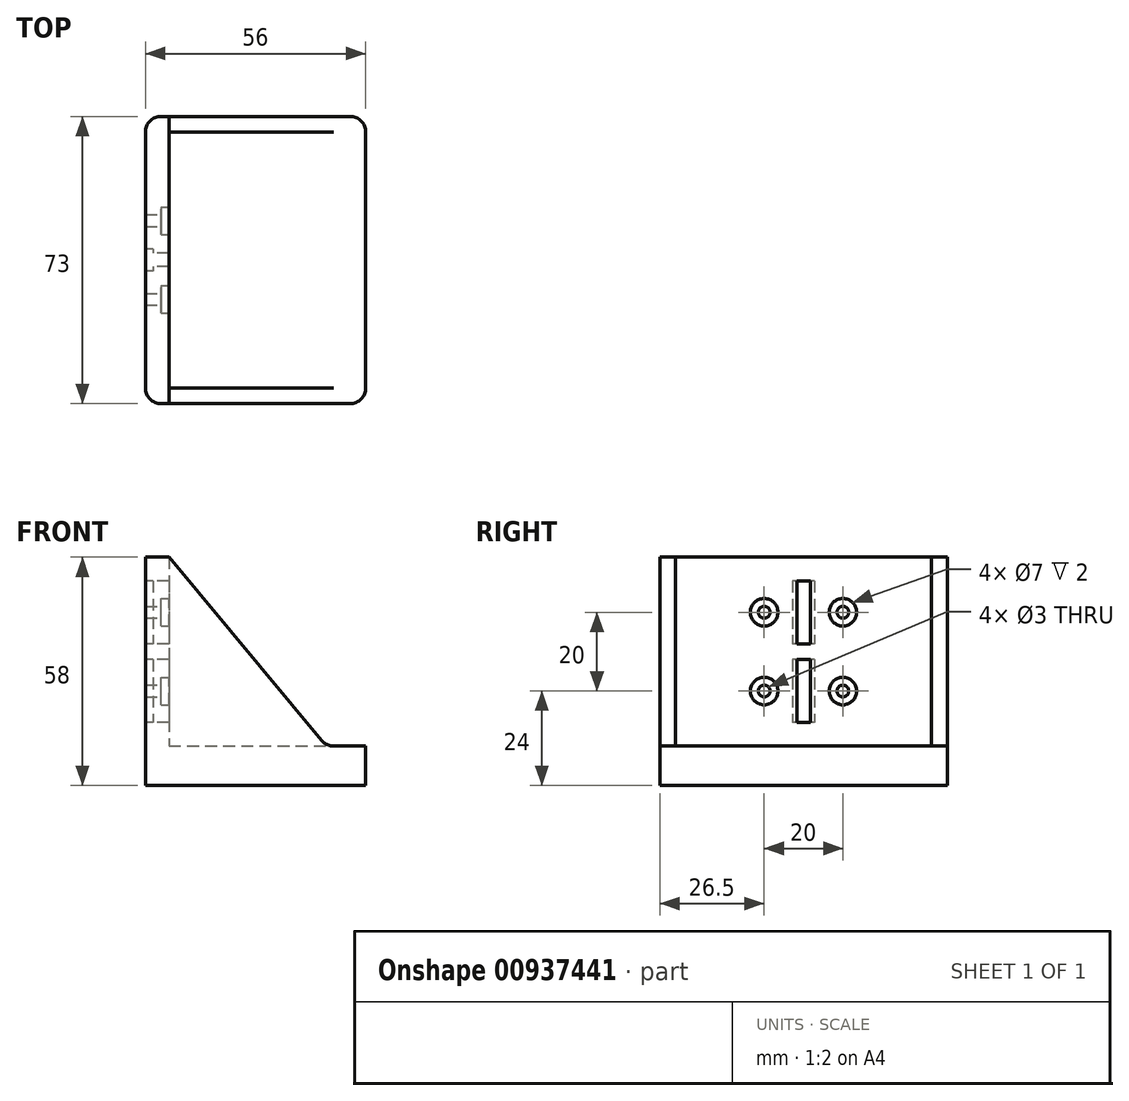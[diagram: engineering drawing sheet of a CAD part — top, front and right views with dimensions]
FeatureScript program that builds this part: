
annotation { "Feature Type Name" : "Feature", "Feature Type Description" : "" }
export const myFeature = defineFeature(function(context is Context, id is Id, definition is map)
    precondition{}
    {
        {
            var Q0;
            Q0=qCreatedBy(makeId("Top.planeOp"),FACE);
            var sketch = newSketch(context, id + "F0", { "sketchPlane" : qUnion([Q0])});
            skLineSegment(sketch, "E0.bottom", {"start": v(0, 73) * mm, "end": v(56, 73) * mm});
            skLineSegment(sketch, "E0.top", {"start": v(0, 0) * mm, "end": v(56, 0) * mm});
            skLineSegment(sketch, "E0.left", {"start": v(0, 73) * mm, "end": v(0, 0) * mm});
            skLineSegment(sketch, "E0.right", {"start": v(56, 73) * mm, "end": v(56, 0) * mm});
            skSolve(sketch);
        }
        {
            var Q0;
            Q0=qSketchRegion(id+"F0",true);
            extrude(context, id + "F1", {"entities" : qUnion([Q0]), "depth" : 10 * mm, "offsetDistance" : 25 * mm});
        }
        {
            var Q0;
            Q0=makeQuery(id+"F1.opExtrude","CAP_FACE",FACE,{"disambiguationData":[OSD([sQuery(id+"F0.wireOp",EDGE,"JcqLtr4a-4iO0-7SYc-JrXt-3wWf4lI9VCyy"),sQuery(id+"F0.wireOp",EDGE,"3zeIyssa-BI9L-WOF6-APSg-kyZtDzQDufFM"),sQuery(id+"F0.wireOp",EDGE,"Hb38dC7V-6ZDo-NrQG-Z8Se-XjxkW8JbUmMz"),sQuery(id+"F0.wireOp",EDGE,"y3aIqdCw-jFc2-MhhD-7X5v-KuRHTVy27k4Q"),sQuery(id+"F0.wireOp",EDGE,"XVNT8TL3-6rPS-E8CT-cUIb-nR5d3DAh4WGq"),sQuery(id+"F0.wireOp",EDGE,"E0.bottom"),sQuery(id+"F0.wireOp",EDGE,"E0.top"),sQuery(id+"F0.wireOp",EDGE,"E0.left"),sQuery(id+"F0.wireOp",EDGE,"E0.right")])],"isStart":false});
            var sketch = newSketch(context, id + "F2", { "sketchPlane" : qUnion([Q0])});
            skLineSegment(sketch, "E1.bottom", {"start": v(0, 73) * mm, "end": v(6, 73) * mm});
            skLineSegment(sketch, "E1.top", {"start": v(0, 0) * mm, "end": v(6, 0) * mm});
            skLineSegment(sketch, "E1.left", {"start": v(0, 73) * mm, "end": v(0, 0) * mm});
            skLineSegment(sketch, "E1.right", {"start": v(6, 73) * mm, "end": v(6, 0) * mm});
            skLineSegment(sketch, "E2.bottom", {"start": v(6, 73) * mm, "end": v(46, 73) * mm});
            skLineSegment(sketch, "E2.top", {"start": v(6, 69) * mm, "end": v(46, 69) * mm});
            skLineSegment(sketch, "E2.left", {"start": v(6, 73) * mm, "end": v(6, 69) * mm});
            skLineSegment(sketch, "E2.right", {"start": v(46, 73) * mm, "end": v(46, 69) * mm});
            skLineSegment(sketch, "E3.bottom", {"start": v(6, 0) * mm, "end": v(46, 0) * mm});
            skLineSegment(sketch, "E3.top", {"start": v(6, 4) * mm, "end": v(46, 4) * mm});
            skLineSegment(sketch, "E3.left", {"start": v(6, 0) * mm, "end": v(6, 4) * mm});
            skLineSegment(sketch, "E3.right", {"start": v(46, 0) * mm, "end": v(46, 4) * mm});
            skSolve(sketch);
        }
        {
            var Q0;
            Q0=qSketchRegion(id+"F2",true);
            extrude(context, id + "F3", {"entities" : qUnion([Q0]), "operationType" : NewBodyOperationType.ADD, "depth" : (25 + 15 + 8) * mm, "offsetDistance" : 25 * mm});
        }
        {
            var Q0;
            Q0=makeQuery(id+"F3.boolean.opBoolean","MERGE",FACE,{"derivedFrom":[makeQuery(id+"F1.opExtrude","SWEPT_FACE",FACE,{"disambiguationData":[OSD([sQuery(id+"F0.wireOp",EDGE,"E0.top")])]}),makeQuery(id+"F3.opExtrude","SWEPT_FACE",FACE,{"disambiguationData":[OSD([sQuery(id+"F2.wireOp",EDGE,"E1.top"),sQuery(id+"F2.wireOp",EDGE,"E3.bottom")])]})]});
            var sketch = newSketch(context, id + "F4", { "sketchPlane" : qUnion([Q0])});
            skLineSegment(sketch, "E4", {"start": v(46, 10) * mm, "end": v(6, 58) * mm});
            skLineSegment(sketch, "E5", {"start": v(6, 58) * mm, "end": v(46, 58) * mm});
            skLineSegment(sketch, "E6", {"start": v(46, 58) * mm, "end": v(46, 10) * mm});
            skSolve(sketch);
        }
        {
            var Q0;
            Q0=qSketchRegion(id+"F4",true);
            extrude(context, id + "F5", {"entities" : qUnion([Q0]), "operationType" : NewBodyOperationType.REMOVE, "endBound" : BoundingType.THROUGH_ALL, "oppositeDirection" : true, "depth" : 25 * mm, "offsetDistance" : 25 * mm});
        }
        {
            var Q0;
            Q0=makeQuery(id+"F3.boolean.opBoolean","MERGE",EDGE,{"derivedFrom":[makeQuery(id+"F1.opExtrude","SWEPT_EDGE",EDGE,{"disambiguationData":[OSD([sQuery(id+"F0.wireOp",EDGE,"E0.top"),sQuery(id+"F0.wireOp",EDGE,"E0.left")])]}),makeQuery(id+"F3.opExtrude","SWEPT_EDGE",EDGE,{"disambiguationData":[OSD([sQuery(id+"F2.wireOp",EDGE,"E1.top"),sQuery(id+"F2.wireOp",EDGE,"E1.left")])]})]});
            var Q1;
            Q1=makeQuery(id+"F1.opExtrude","SWEPT_EDGE",EDGE,{"disambiguationData":[OSD([sQuery(id+"F0.wireOp",EDGE,"E0.top"),sQuery(id+"F0.wireOp",EDGE,"E0.right")])]});
            var Q2;
            Q2=makeQuery(id+"F5.boolean.opBoolean","MERGE",EDGE,{"derivedFrom":[makeQuery(id+"F3.opExtrude","CAP_EDGE",EDGE,{"disambiguationData":[OSD([sQuery(id+"F2.wireOp",EDGE,"E3.right")])],"isStart":true})],"fromTools":[makeQuery(id+"F5.opExtrude","SWEPT_EDGE",EDGE,{"disambiguationData":[OSD([sQuery(id+"F0.wireOp",EDGE,"E0.top"),sQuery(id+"F4.wireOp",EDGE,"E4"),sQuery(id+"F4.wireOp",EDGE,"E6")])]})]});
            var Q3;
            Q3=makeQuery(id+"F5.boolean.opBoolean","MERGE",EDGE,{"derivedFrom":[makeQuery(id+"F3.opExtrude","CAP_EDGE",EDGE,{"disambiguationData":[OSD([sQuery(id+"F2.wireOp",EDGE,"E2.right")])],"isStart":true})],"fromTools":[makeQuery(id+"F5.opExtrude","SWEPT_EDGE",EDGE,{"disambiguationData":[OSD([sQuery(id+"F0.wireOp",EDGE,"E0.top"),sQuery(id+"F4.wireOp",EDGE,"E4"),sQuery(id+"F4.wireOp",EDGE,"E6")])]})]});
            var Q4;
            Q4=makeQuery(id+"F1.opExtrude","SWEPT_EDGE",EDGE,{"disambiguationData":[OSD([sQuery(id+"F0.wireOp",EDGE,"E0.bottom"),sQuery(id+"F0.wireOp",EDGE,"E0.right")])]});
            var Q5;
            Q5=makeQuery(id+"F3.boolean.opBoolean","MERGE",EDGE,{"derivedFrom":[makeQuery(id+"F1.opExtrude","SWEPT_EDGE",EDGE,{"disambiguationData":[OSD([sQuery(id+"F0.wireOp",EDGE,"E0.bottom"),sQuery(id+"F0.wireOp",EDGE,"E0.left")])]}),makeQuery(id+"F3.opExtrude","SWEPT_EDGE",EDGE,{"disambiguationData":[OSD([sQuery(id+"F2.wireOp",EDGE,"E1.bottom"),sQuery(id+"F2.wireOp",EDGE,"E1.left")])]})]});
            fillet(context, id + "F6", {"entities" : qUnion([Q0, Q1, Q2, Q3, Q4, Q5]), "radius" : 4 * mm, "tangentPropagation" : true, "allowEdgeOverflow" : false});
        }
        {
            var Q0;
            Q0=makeQuery(id+"F3.boolean.opBoolean","MERGE",FACE,{"derivedFrom":[makeQuery(id+"F1.opExtrude","SWEPT_FACE",FACE,{"disambiguationData":[OSD([sQuery(id+"F0.wireOp",EDGE,"E0.left")])]}),makeQuery(id+"F3.opExtrude","SWEPT_FACE",FACE,{"disambiguationData":[OSD([sQuery(id+"F2.wireOp",EDGE,"E1.left")])]})]});
            var sketch = newSketch(context, id + "F7", { "sketchPlane" : qUnion([Q0])});
            skLineSegment(sketch, "E7", {"start": v(-36.5, 52) * mm, "end": v(-36.5, 16) * mm, "construction": true});
            skLineSegment(sketch, "E8", {"start": v(-38.22, 52) * mm, "end": v(-38.22, 16) * mm});
            skLineSegment(sketch, "E9", {"start": v(-34.77, 52) * mm, "end": v(-34.77, 16) * mm});
            skLineSegment(sketch, "E10.bottom", {"start": v(-39.26, 36) * mm, "end": v(-33.74, 36) * mm});
            skLineSegment(sketch, "E10.top", {"start": v(-39.26, 32) * mm, "end": v(-33.74, 32) * mm});
            skLineSegment(sketch, "E10.left", {"start": v(-39.26, 36) * mm, "end": v(-39.26, 32) * mm});
            skLineSegment(sketch, "E10.right", {"start": v(-33.74, 36) * mm, "end": v(-33.74, 32) * mm});
            skLineSegment(sketch, "E11", {"start": v(-36.5, 34) * mm, "end": v(-39.26, 34) * mm, "construction": true});
            skLineSegment(sketch, "E12", {"start": v(-34.77, 52) * mm, "end": v(-38.22, 52) * mm});
            skLineSegment(sketch, "E13", {"start": v(-34.77, 16) * mm, "end": v(-38.22, 16) * mm});
            skLineSegment(sketch, "E14.bottom", {"start": v(-39.26, 52) * mm, "end": v(-33.74, 52) * mm});
            skLineSegment(sketch, "E14.top", {"start": v(-39.26, 16) * mm, "end": v(-33.74, 16) * mm});
            skLineSegment(sketch, "E14.left", {"start": v(-39.26, 52) * mm, "end": v(-39.26, 16) * mm});
            skLineSegment(sketch, "E14.right", {"start": v(-33.74, 52) * mm, "end": v(-33.74, 16) * mm});
            skLineSegment(sketch, "E15", {"start": v(-39.26, 34) * mm, "end": v(-39.26, 34) * mm});
            skLineSegment(sketch, "E16", {"start": v(-36.5, 58) * mm, "end": v(-36.5, 52) * mm, "construction": true});
            skSolve(sketch);
        }
        {
            var Q0;
            {var subQ0=sQuery(id+"F7.wireOp",EDGE,"E14.bottom");var subQ1=sQuery(id+"F7.wireOp",EDGE,"E8");var subQ2=makeQuery(id+"F7.imprint","INTERSECT",VERTEX,{"derivedFrom":[subQ1,subQ0]});Q0=makeQuery(id+"F7.imprint","IMPRINT",FACE,{"disambiguationData":[TD([[makeQuery(id+"F7.imprint","IMPRINT",EDGE,{"disambiguationData":[TD([[subQ2,-1.0]])],"derivedFrom":subQ1}),-1.0]])]});}
            var Q1;
            {var subQ0=sQuery(id+"F7.wireOp",EDGE,"E14.bottom");var subQ1=sQuery(id+"F7.wireOp",EDGE,"E9");var subQ2=makeQuery(id+"F7.imprint","INTERSECT",VERTEX,{"derivedFrom":[subQ1,subQ0]});Q1=makeQuery(id+"F7.imprint","IMPRINT",FACE,{"disambiguationData":[TD([[makeQuery(id+"F7.imprint","IMPRINT",EDGE,{"disambiguationData":[TD([[subQ2,-1.0]])],"derivedFrom":subQ1}),1.0]])]});}
            var Q2;
            {var subQ0=sQuery(id+"F7.wireOp",EDGE,"E14.top");var subQ1=sQuery(id+"F7.wireOp",EDGE,"E9");var subQ2=makeQuery(id+"F7.imprint","INTERSECT",VERTEX,{"derivedFrom":[subQ1,subQ0]});Q2=makeQuery(id+"F7.imprint","IMPRINT",FACE,{"disambiguationData":[TD([[makeQuery(id+"F7.imprint","IMPRINT",EDGE,{"disambiguationData":[TD([[subQ2,1.0]])],"derivedFrom":subQ1}),1.0]])]});}
            var Q3;
            {var subQ0=sQuery(id+"F7.wireOp",EDGE,"E14.top");var subQ1=sQuery(id+"F7.wireOp",EDGE,"E8");var subQ2=makeQuery(id+"F7.imprint","INTERSECT",VERTEX,{"derivedFrom":[subQ1,subQ0]});Q3=makeQuery(id+"F7.imprint","IMPRINT",FACE,{"disambiguationData":[TD([[makeQuery(id+"F7.imprint","IMPRINT",EDGE,{"disambiguationData":[TD([[subQ2,1.0]])],"derivedFrom":subQ1}),-1.0]])]});}
            extrude(context, id + "F8", {"entities" : qUnion([Q0, Q1, Q2, Q3]), "operationType" : NewBodyOperationType.REMOVE, "oppositeDirection" : true, "depth" : 2 * mm, "offsetDistance" : 25 * mm});
        }
        {
            var Q0;
            {var subQ0=sQuery(id+"F7.wireOp",EDGE,"E14.bottom");var subQ1=sQuery(id+"F7.wireOp",EDGE,"E8");var subQ2=makeQuery(id+"F7.imprint","INTERSECT",VERTEX,{"derivedFrom":[subQ1,subQ0]});Q0=makeQuery(id+"F7.imprint","IMPRINT",FACE,{"disambiguationData":[TD([[makeQuery(id+"F7.imprint","IMPRINT",EDGE,{"disambiguationData":[TD([[subQ2,-1.0]])],"derivedFrom":subQ1}),1.0]])]});}
            var Q1;
            {var subQ0=sQuery(id+"F7.wireOp",EDGE,"E14.top");var subQ1=sQuery(id+"F7.wireOp",EDGE,"E8");var subQ2=makeQuery(id+"F7.imprint","INTERSECT",VERTEX,{"derivedFrom":[subQ1,subQ0]});Q1=makeQuery(id+"F7.imprint","IMPRINT",FACE,{"disambiguationData":[TD([[makeQuery(id+"F7.imprint","IMPRINT",EDGE,{"disambiguationData":[TD([[subQ2,1.0]])],"derivedFrom":subQ1}),1.0]])]});}
            extrude(context, id + "F9", {"entities" : qUnion([Q0, Q1]), "operationType" : NewBodyOperationType.REMOVE, "endBound" : BoundingType.UP_TO_NEXT, "oppositeDirection" : true, "depth" : 25 * mm, "offsetDistance" : 25 * mm});
        }
        {
            var Q0;
            Q0=makeQuery(id+"F3.opExtrude","SWEPT_FACE",FACE,{"disambiguationData":[OSD([sQuery(id+"F2.wireOp",EDGE,"E1.right")])]});
            var sketch = newSketch(context, id + "F10", { "sketchPlane" : qUnion([Q0])});
            skLineSegment(sketch, "E17.bottom", {"start": v(26.5, 44) * mm, "end": v(46.5, 44) * mm, "construction": true});
            skLineSegment(sketch, "E17.top", {"start": v(26.5, 24) * mm, "end": v(46.5, 24) * mm, "construction": true});
            skLineSegment(sketch, "E17.left", {"start": v(26.5, 44) * mm, "end": v(26.5, 24) * mm, "construction": true});
            skLineSegment(sketch, "E17.right", {"start": v(46.5, 44) * mm, "end": v(46.5, 24) * mm, "construction": true});
            skCircle(sketch, "E18", {"center": v(26.5, 44) * mm, "radius": 1.5 * mm});
            skCircle(sketch, "E19", {"center": v(46.5, 44) * mm, "radius": 1.5 * mm});
            skCircle(sketch, "E20", {"center": v(46.5, 24) * mm, "radius": 1.5 * mm});
            skCircle(sketch, "E21", {"center": v(26.5, 24) * mm, "radius": 1.5 * mm});
            skCircle(sketch, "E22", {"center": v(26.5, 44) * mm, "radius": 3.5 * mm});
            skCircle(sketch, "E23", {"center": v(46.5, 44) * mm, "radius": 3.5 * mm});
            skCircle(sketch, "E24", {"center": v(46.5, 24) * mm, "radius": 3.5 * mm});
            skCircle(sketch, "E25", {"center": v(26.5, 24) * mm, "radius": 3.5 * mm});
            skLineSegment(sketch, "E26", {"start": v(36.5, 58) * mm, "end": v(36.5, 44) * mm, "construction": true});
            skSolve(sketch);
        }
        {
            var Q0;
            Q0=qSketchRegion(id+"F10",true);
            extrude(context, id + "F11", {"entities" : qUnion([Q0]), "operationType" : NewBodyOperationType.REMOVE, "oppositeDirection" : true, "depth" : 2 * mm, "offsetDistance" : 25 * mm});
        }
        {
            var Q0;
            Q0=makeQuery(id+"F10.imprint","IMPRINT",FACE,{"disambiguationData":[TD([[makeQuery(id+"F10.imprint","IMPRINT",EDGE,{"derivedFrom":sQuery(id+"F10.wireOp",EDGE,"E18")}),1.0]])]});
            var Q1;
            Q1=makeQuery(id+"F10.imprint","IMPRINT",FACE,{"disambiguationData":[TD([[makeQuery(id+"F10.imprint","IMPRINT",EDGE,{"derivedFrom":sQuery(id+"F10.wireOp",EDGE,"E19")}),1.0]])]});
            var Q2;
            Q2=makeQuery(id+"F10.imprint","IMPRINT",FACE,{"disambiguationData":[TD([[makeQuery(id+"F10.imprint","IMPRINT",EDGE,{"derivedFrom":sQuery(id+"F10.wireOp",EDGE,"E20")}),1.0]])]});
            var Q3;
            Q3=makeQuery(id+"F10.imprint","IMPRINT",FACE,{"disambiguationData":[TD([[makeQuery(id+"F10.imprint","IMPRINT",EDGE,{"derivedFrom":sQuery(id+"F10.wireOp",EDGE,"E21")}),1.0]])]});
            extrude(context, id + "F12", {"entities" : qUnion([Q0, Q1, Q2, Q3]), "operationType" : NewBodyOperationType.REMOVE, "endBound" : BoundingType.UP_TO_NEXT, "oppositeDirection" : true, "depth" : 25 * mm, "offsetDistance" : 25 * mm});
        }
    });
